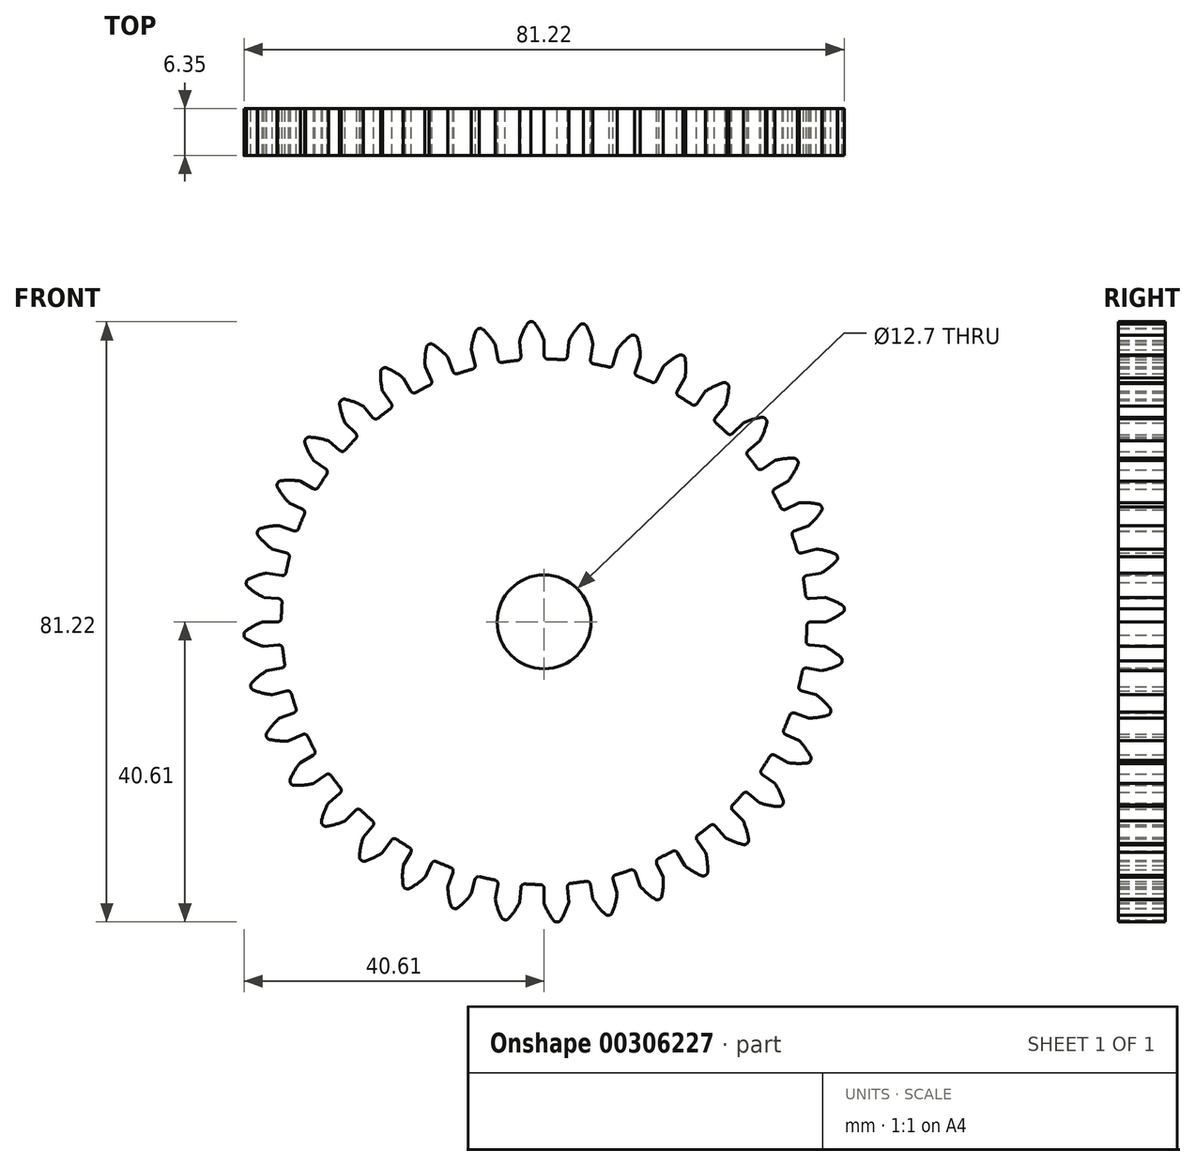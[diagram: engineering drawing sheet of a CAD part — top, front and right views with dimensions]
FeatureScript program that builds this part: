
annotation { "Feature Type Name" : "Feature", "Feature Type Description" : "" }
export const myFeature = defineFeature(function(context is Context, id is Id, definition is map)
    precondition{}
    {
        {
            var Q0;
            Q0=qCreatedBy(makeId("Front.planeOp"),FACE);
            var sketch = newSketch(context, id + "F0", { "sketchPlane" : qUnion([Q0])});
            skArc(sketch, "E0", {"start": v(-3.6, 35.38) * mm, "mid": v(1.55, -35.53) * mm, "end": v(0.5, 35.56) * mm});
            skLineSegment(sketch, "E1", {"start": v(0, 0) * mm, "end": v(-2.87, 65.75) * mm, "construction": true});
            skArc(sketch, "E2", {"start": v(0, 38.1) * mm, "mid": v(-0.56, 39.3) * mm, "end": v(-1.28, 40.41) * mm});
            skLineSegment(sketch, "E3", {"start": v(-1.69, 40.61) * mm, "end": v(-1.77, 40.61) * mm});
            skLineSegment(sketch, "E4", {"start": v(0, 38.1) * mm, "end": v(0, 36.06) * mm});
            skLineSegment(sketch, "E5.MirrorCS", {"start": v(-1.86, 40.6) * mm, "end": v(-1.77, 40.61) * mm});
            skArc(sketch, "E6.MirrorCS", {"start": v(-3.32, 37.96) * mm, "mid": v(-2.87, 39.2) * mm, "end": v(-2.24, 40.37) * mm});
            skLineSegment(sketch, "E7.MirrorCS", {"start": v(-3.32, 37.96) * mm, "end": v(-3.14, 35.93) * mm});
            skPoint(sketch, "E8.orphan", {"position": v(-2.9, 33.08) * mm});
            skPoint(sketch, "E9.orphan", {"position": v(0, 33.2) * mm});
            skPoint(sketch, "E10.visualSharp", {"position": v(-3.1, 35.42) * mm});
            skArc(sketch, "E10.filletArc", {"start": v(-3.6, 35.38) * mm, "mid": v(-3.26, 35.56) * mm, "end": v(-3.14, 35.93) * mm});
            skPoint(sketch, "E11.visualSharp", {"position": v(0, 35.56) * mm});
            skArc(sketch, "E11.filletArc", {"start": v(0, 36.06) * mm, "mid": v(0.15, 35.7) * mm, "end": v(0.5, 35.56) * mm});
            skPoint(sketch, "E12.visualSharp", {"position": v(-2.1, 40.59) * mm});
            skArc(sketch, "E12.filletArc", {"start": v(-1.86, 40.6) * mm, "mid": v(-2.08, 40.53) * mm, "end": v(-2.24, 40.37) * mm});
            skPoint(sketch, "E13.visualSharp", {"position": v(-1.44, 40.61) * mm});
            skArc(sketch, "E13.filletArc", {"start": v(-1.28, 40.41) * mm, "mid": v(-1.46, 40.56) * mm, "end": v(-1.69, 40.61) * mm});
            skArc(sketch, "E14.1.0", {"start": v(-9.69, 34.22) * mm, "mid": v(-9.38, 34.45) * mm, "end": v(-9.33, 34.84) * mm});
            skLineSegment(sketch, "E14.1.1", {"start": v(-9.86, 36.8) * mm, "end": v(-9.33, 34.84) * mm});
            skArc(sketch, "E14.1.2", {"start": v(-9.86, 36.8) * mm, "mid": v(-9.63, 38.1) * mm, "end": v(-9.22, 39.37) * mm});
            skArc(sketch, "E14.1.3", {"start": v(-6.62, 37.52) * mm, "mid": v(-7.38, 38.6) * mm, "end": v(-8.28, 39.58) * mm});
            skArc(sketch, "E14.1.4", {"start": v(-6.26, 35.52) * mm, "mid": v(-6.06, 35.2) * mm, "end": v(-5.68, 35.1) * mm});
            skLineSegment(sketch, "E14.1.5", {"start": v(-6.62, 37.52) * mm, "end": v(-6.26, 35.52) * mm});
            skArc(sketch, "E14.1.6", {"start": v(-8.88, 39.67) * mm, "mid": v(-9.09, 39.56) * mm, "end": v(-9.22, 39.37) * mm});
            skLineSegment(sketch, "E14.1.7", {"start": v(-8.88, 39.67) * mm, "end": v(-8.8, 39.69) * mm});
            skLineSegment(sketch, "E14.1.8", {"start": v(-8.72, 39.7) * mm, "end": v(-8.8, 39.69) * mm});
            skArc(sketch, "E14.1.9", {"start": v(-8.28, 39.58) * mm, "mid": v(-8.48, 39.7) * mm, "end": v(-8.72, 39.7) * mm});
            skArc(sketch, "E14.2.0", {"start": v(-15.48, 32.01) * mm, "mid": v(-15.22, 32.3) * mm, "end": v(-15.24, 32.69) * mm});
            skLineSegment(sketch, "E14.2.1", {"start": v(-16.1, 34.53) * mm, "end": v(-15.24, 32.69) * mm});
            skArc(sketch, "E14.2.2", {"start": v(-16.1, 34.53) * mm, "mid": v(-16.1, 35.86) * mm, "end": v(-15.92, 37.17) * mm});
            skArc(sketch, "E14.2.3", {"start": v(-13.03, 35.8) * mm, "mid": v(-13.97, 36.74) * mm, "end": v(-15.03, 37.54) * mm});
            skArc(sketch, "E14.2.4", {"start": v(-12.33, 33.89) * mm, "mid": v(-12.08, 33.6) * mm, "end": v(-11.7, 33.58) * mm});
            skLineSegment(sketch, "E14.2.5", {"start": v(-13.03, 35.8) * mm, "end": v(-12.33, 33.89) * mm});
            skArc(sketch, "E14.2.6", {"start": v(-15.63, 37.52) * mm, "mid": v(-15.82, 37.38) * mm, "end": v(-15.92, 37.17) * mm});
            skLineSegment(sketch, "E14.2.7", {"start": v(-15.63, 37.52) * mm, "end": v(-15.56, 37.56) * mm});
            skLineSegment(sketch, "E14.2.8", {"start": v(-15.48, 37.59) * mm, "end": v(-15.56, 37.56) * mm});
            skArc(sketch, "E14.2.9", {"start": v(-15.03, 37.54) * mm, "mid": v(-15.25, 37.62) * mm, "end": v(-15.48, 37.59) * mm});
            skArc(sketch, "E14.3.0", {"start": v(-20.8, 28.84) * mm, "mid": v(-20.6, 29.17) * mm, "end": v(-20.69, 29.54) * mm});
            skLineSegment(sketch, "E14.3.1", {"start": v(-21.85, 31.2) * mm, "end": v(-20.69, 29.54) * mm});
            skArc(sketch, "E14.3.2", {"start": v(-21.85, 31.2) * mm, "mid": v(-22.08, 32.51) * mm, "end": v(-22.13, 33.84) * mm});
            skArc(sketch, "E14.3.3", {"start": v(-19.05, 33) * mm, "mid": v(-20.14, 33.76) * mm, "end": v(-21.32, 34.36) * mm});
            skArc(sketch, "E14.3.4", {"start": v(-18.03, 31.23) * mm, "mid": v(-17.73, 31) * mm, "end": v(-17.34, 31.04) * mm});
            skLineSegment(sketch, "E14.3.5", {"start": v(-19.05, 33) * mm, "end": v(-18.03, 31.23) * mm});
            skArc(sketch, "E14.3.6", {"start": v(-21.91, 34.24) * mm, "mid": v(-22.07, 34.06) * mm, "end": v(-22.13, 33.84) * mm});
            skLineSegment(sketch, "E14.3.7", {"start": v(-21.91, 34.24) * mm, "end": v(-21.84, 34.29) * mm});
            skLineSegment(sketch, "E14.3.8", {"start": v(-21.77, 34.33) * mm, "end": v(-21.84, 34.29) * mm});
            skArc(sketch, "E14.3.9", {"start": v(-21.32, 34.36) * mm, "mid": v(-21.55, 34.4) * mm, "end": v(-21.77, 34.33) * mm});
            skArc(sketch, "E14.4.0", {"start": v(-25.5, 24.79) * mm, "mid": v(-25.35, 25.15) * mm, "end": v(-25.5, 25.5) * mm});
            skLineSegment(sketch, "E14.4.1", {"start": v(-26.94, 26.94) * mm, "end": v(-25.5, 25.5) * mm});
            skArc(sketch, "E14.4.2", {"start": v(-26.94, 26.94) * mm, "mid": v(-27.4, 28.19) * mm, "end": v(-27.67, 29.48) * mm});
            skArc(sketch, "E14.4.3", {"start": v(-24.5, 29.19) * mm, "mid": v(-25.7, 29.75) * mm, "end": v(-26.96, 30.13) * mm});
            skArc(sketch, "E14.4.4", {"start": v(-23.18, 27.63) * mm, "mid": v(-22.84, 27.45) * mm, "end": v(-22.47, 27.56) * mm});
            skLineSegment(sketch, "E14.4.5", {"start": v(-24.5, 29.19) * mm, "end": v(-23.18, 27.63) * mm});
            skArc(sketch, "E14.4.6", {"start": v(-27.53, 29.91) * mm, "mid": v(-27.65, 29.71) * mm, "end": v(-27.67, 29.48) * mm});
            skLineSegment(sketch, "E14.4.7", {"start": v(-27.53, 29.91) * mm, "end": v(-27.46, 29.97) * mm});
            skLineSegment(sketch, "E14.4.8", {"start": v(-27.4, 30.03) * mm, "end": v(-27.46, 29.97) * mm});
            skArc(sketch, "E14.4.9", {"start": v(-26.96, 30.13) * mm, "mid": v(-27.2, 30.13) * mm, "end": v(-27.4, 30.03) * mm});
            skArc(sketch, "E14.5.0", {"start": v(-29.41, 19.98) * mm, "mid": v(-29.33, 20.36) * mm, "end": v(-29.54, 20.69) * mm});
            skLineSegment(sketch, "E14.5.1", {"start": v(-31.2, 21.85) * mm, "end": v(-29.54, 20.69) * mm});
            skArc(sketch, "E14.5.2", {"start": v(-31.2, 21.85) * mm, "mid": v(-31.87, 23) * mm, "end": v(-32.37, 24.23) * mm});
            skArc(sketch, "E14.5.3", {"start": v(-29.19, 24.5) * mm, "mid": v(-30.47, 24.83) * mm, "end": v(-31.78, 25) * mm});
            skArc(sketch, "E14.5.4", {"start": v(-27.63, 23.18) * mm, "mid": v(-27.26, 23.06) * mm, "end": v(-26.92, 23.24) * mm});
            skLineSegment(sketch, "E14.5.5", {"start": v(-29.19, 24.5) * mm, "end": v(-27.63, 23.18) * mm});
            skArc(sketch, "E14.5.6", {"start": v(-32.3, 24.68) * mm, "mid": v(-32.39, 24.46) * mm, "end": v(-32.37, 24.23) * mm});
            skLineSegment(sketch, "E14.5.7", {"start": v(-32.3, 24.68) * mm, "end": v(-32.25, 24.75) * mm});
            skLineSegment(sketch, "E14.5.8", {"start": v(-32.2, 24.81) * mm, "end": v(-32.25, 24.75) * mm});
            skArc(sketch, "E14.5.9", {"start": v(-31.78, 25) * mm, "mid": v(-32.01, 24.95) * mm, "end": v(-32.2, 24.81) * mm});
            skArc(sketch, "E14.6.0", {"start": v(-32.44, 14.57) * mm, "mid": v(-32.42, 14.96) * mm, "end": v(-32.69, 15.24) * mm});
            skLineSegment(sketch, "E14.6.1", {"start": v(-34.53, 16.1) * mm, "end": v(-32.69, 15.24) * mm});
            skArc(sketch, "E14.6.2", {"start": v(-34.53, 16.1) * mm, "mid": v(-35.38, 17.12) * mm, "end": v(-36.08, 18.24) * mm});
            skArc(sketch, "E14.6.3", {"start": v(-33, 19.05) * mm, "mid": v(-34.32, 19.16) * mm, "end": v(-35.64, 19.1) * mm});
            skArc(sketch, "E14.6.4", {"start": v(-31.23, 18.03) * mm, "mid": v(-30.85, 17.98) * mm, "end": v(-30.54, 18.21) * mm});
            skLineSegment(sketch, "E14.6.5", {"start": v(-33, 19.05) * mm, "end": v(-31.23, 18.03) * mm});
            skArc(sketch, "E14.6.6", {"start": v(-36.1, 18.7) * mm, "mid": v(-36.14, 18.47) * mm, "end": v(-36.08, 18.24) * mm});
            skLineSegment(sketch, "E14.6.7", {"start": v(-36.1, 18.7) * mm, "end": v(-36.06, 18.77) * mm});
            skLineSegment(sketch, "E14.6.8", {"start": v(-36.02, 18.85) * mm, "end": v(-36.06, 18.77) * mm});
            skArc(sketch, "E14.6.9", {"start": v(-35.64, 19.1) * mm, "mid": v(-35.86, 19.01) * mm, "end": v(-36.02, 18.85) * mm});
            skArc(sketch, "E14.7.0", {"start": v(-34.47, 8.72) * mm, "mid": v(-34.53, 9.1) * mm, "end": v(-34.84, 9.33) * mm});
            skLineSegment(sketch, "E14.7.1", {"start": v(-36.8, 9.86) * mm, "end": v(-34.84, 9.33) * mm});
            skArc(sketch, "E14.7.2", {"start": v(-36.8, 9.86) * mm, "mid": v(-37.82, 10.71) * mm, "end": v(-38.7, 11.7) * mm});
            skArc(sketch, "E14.7.3", {"start": v(-35.8, 13.03) * mm, "mid": v(-37.12, 12.91) * mm, "end": v(-38.41, 12.62) * mm});
            skArc(sketch, "E14.7.4", {"start": v(-33.89, 12.33) * mm, "mid": v(-33.5, 12.35) * mm, "end": v(-33.24, 12.63) * mm});
            skLineSegment(sketch, "E14.7.5", {"start": v(-35.8, 13.03) * mm, "end": v(-33.89, 12.33) * mm});
            skArc(sketch, "E14.7.6", {"start": v(-38.8, 12.14) * mm, "mid": v(-38.8, 11.9) * mm, "end": v(-38.7, 11.7) * mm});
            skLineSegment(sketch, "E14.7.7", {"start": v(-38.8, 12.14) * mm, "end": v(-38.77, 12.22) * mm});
            skLineSegment(sketch, "E14.7.8", {"start": v(-38.74, 12.3) * mm, "end": v(-38.77, 12.22) * mm});
            skArc(sketch, "E14.7.9", {"start": v(-38.41, 12.62) * mm, "mid": v(-38.61, 12.5) * mm, "end": v(-38.74, 12.3) * mm});
            skArc(sketch, "E14.8.0", {"start": v(-35.46, 2.6) * mm, "mid": v(-35.58, 2.97) * mm, "end": v(-35.93, 3.14) * mm});
            skLineSegment(sketch, "E14.8.1", {"start": v(-37.96, 3.32) * mm, "end": v(-35.93, 3.14) * mm});
            skArc(sketch, "E14.8.2", {"start": v(-37.96, 3.32) * mm, "mid": v(-39.1, 3.98) * mm, "end": v(-40.15, 4.8) * mm});
            skArc(sketch, "E14.8.3", {"start": v(-37.52, 6.62) * mm, "mid": v(-38.8, 6.27) * mm, "end": v(-40.02, 5.75) * mm});
            skArc(sketch, "E14.8.4", {"start": v(-35.52, 6.26) * mm, "mid": v(-35.14, 6.34) * mm, "end": v(-34.93, 6.67) * mm});
            skLineSegment(sketch, "E14.8.5", {"start": v(-37.52, 6.62) * mm, "end": v(-35.52, 6.26) * mm});
            skArc(sketch, "E14.8.6", {"start": v(-40.31, 5.22) * mm, "mid": v(-40.28, 5) * mm, "end": v(-40.15, 4.8) * mm});
            skLineSegment(sketch, "E14.8.7", {"start": v(-40.31, 5.22) * mm, "end": v(-40.3, 5.3) * mm});
            skLineSegment(sketch, "E14.8.8", {"start": v(-40.3, 5.4) * mm, "end": v(-40.3, 5.3) * mm});
            skArc(sketch, "E14.8.9", {"start": v(-40.02, 5.75) * mm, "mid": v(-40.2, 5.6) * mm, "end": v(-40.3, 5.4) * mm});
            skArc(sketch, "E14.9.0", {"start": v(-35.38, -3.6) * mm, "mid": v(-35.56, -3.26) * mm, "end": v(-35.93, -3.14) * mm});
            skLineSegment(sketch, "E14.9.1", {"start": v(-37.96, -3.32) * mm, "end": v(-35.93, -3.14) * mm});
            skArc(sketch, "E14.9.2", {"start": v(-37.96, -3.32) * mm, "mid": v(-39.2, -2.87) * mm, "end": v(-40.37, -2.24) * mm});
            skArc(sketch, "E14.9.3", {"start": v(-38.1, 0) * mm, "mid": v(-39.3, -0.56) * mm, "end": v(-40.41, -1.28) * mm});
            skArc(sketch, "E14.9.4", {"start": v(-36.06, 0) * mm, "mid": v(-35.7, 0.15) * mm, "end": v(-35.56, 0.5) * mm});
            skLineSegment(sketch, "E14.9.5", {"start": v(-38.1, 0) * mm, "end": v(-36.06, 0) * mm});
            skArc(sketch, "E14.9.6", {"start": v(-40.6, -1.86) * mm, "mid": v(-40.53, -2.08) * mm, "end": v(-40.37, -2.24) * mm});
            skLineSegment(sketch, "E14.9.7", {"start": v(-40.6, -1.86) * mm, "end": v(-40.61, -1.77) * mm});
            skLineSegment(sketch, "E14.9.8", {"start": v(-40.61, -1.69) * mm, "end": v(-40.61, -1.77) * mm});
            skArc(sketch, "E14.9.9", {"start": v(-40.41, -1.28) * mm, "mid": v(-40.56, -1.46) * mm, "end": v(-40.61, -1.69) * mm});
            skArc(sketch, "E14.10.0", {"start": v(-34.22, -9.69) * mm, "mid": v(-34.45, -9.38) * mm, "end": v(-34.84, -9.33) * mm});
            skLineSegment(sketch, "E14.10.1", {"start": v(-36.8, -9.86) * mm, "end": v(-34.84, -9.33) * mm});
            skArc(sketch, "E14.10.2", {"start": v(-36.8, -9.86) * mm, "mid": v(-38.1, -9.63) * mm, "end": v(-39.37, -9.22) * mm});
            skArc(sketch, "E14.10.3", {"start": v(-37.52, -6.62) * mm, "mid": v(-38.6, -7.38) * mm, "end": v(-39.58, -8.28) * mm});
            skArc(sketch, "E14.10.4", {"start": v(-35.52, -6.26) * mm, "mid": v(-35.2, -6.06) * mm, "end": v(-35.1, -5.68) * mm});
            skLineSegment(sketch, "E14.10.5", {"start": v(-37.52, -6.62) * mm, "end": v(-35.52, -6.26) * mm});
            skArc(sketch, "E14.10.6", {"start": v(-39.67, -8.88) * mm, "mid": v(-39.56, -9.09) * mm, "end": v(-39.37, -9.22) * mm});
            skLineSegment(sketch, "E14.10.7", {"start": v(-39.67, -8.88) * mm, "end": v(-39.69, -8.8) * mm});
            skLineSegment(sketch, "E14.10.8", {"start": v(-39.7, -8.72) * mm, "end": v(-39.69, -8.8) * mm});
            skArc(sketch, "E14.10.9", {"start": v(-39.58, -8.28) * mm, "mid": v(-39.7, -8.48) * mm, "end": v(-39.7, -8.72) * mm});
            skArc(sketch, "E14.11.0", {"start": v(-32.01, -15.48) * mm, "mid": v(-32.3, -15.22) * mm, "end": v(-32.69, -15.24) * mm});
            skLineSegment(sketch, "E14.11.1", {"start": v(-34.53, -16.1) * mm, "end": v(-32.69, -15.24) * mm});
            skArc(sketch, "E14.11.2", {"start": v(-34.53, -16.1) * mm, "mid": v(-35.86, -16.1) * mm, "end": v(-37.17, -15.92) * mm});
            skArc(sketch, "E14.11.3", {"start": v(-35.8, -13.03) * mm, "mid": v(-36.74, -13.97) * mm, "end": v(-37.54, -15.03) * mm});
            skArc(sketch, "E14.11.4", {"start": v(-33.89, -12.33) * mm, "mid": v(-33.6, -12.08) * mm, "end": v(-33.58, -11.7) * mm});
            skLineSegment(sketch, "E14.11.5", {"start": v(-35.8, -13.03) * mm, "end": v(-33.89, -12.33) * mm});
            skArc(sketch, "E14.11.6", {"start": v(-37.52, -15.63) * mm, "mid": v(-37.38, -15.82) * mm, "end": v(-37.17, -15.92) * mm});
            skLineSegment(sketch, "E14.11.7", {"start": v(-37.52, -15.63) * mm, "end": v(-37.56, -15.56) * mm});
            skLineSegment(sketch, "E14.11.8", {"start": v(-37.59, -15.48) * mm, "end": v(-37.56, -15.56) * mm});
            skArc(sketch, "E14.11.9", {"start": v(-37.54, -15.03) * mm, "mid": v(-37.62, -15.25) * mm, "end": v(-37.59, -15.48) * mm});
            skArc(sketch, "E14.12.0", {"start": v(-28.84, -20.8) * mm, "mid": v(-29.17, -20.6) * mm, "end": v(-29.54, -20.69) * mm});
            skLineSegment(sketch, "E14.12.1", {"start": v(-31.2, -21.85) * mm, "end": v(-29.54, -20.69) * mm});
            skArc(sketch, "E14.12.2", {"start": v(-31.2, -21.85) * mm, "mid": v(-32.51, -22.08) * mm, "end": v(-33.84, -22.13) * mm});
            skArc(sketch, "E14.12.3", {"start": v(-33, -19.05) * mm, "mid": v(-33.76, -20.14) * mm, "end": v(-34.36, -21.32) * mm});
            skArc(sketch, "E14.12.4", {"start": v(-31.23, -18.03) * mm, "mid": v(-31, -17.73) * mm, "end": v(-31.04, -17.34) * mm});
            skLineSegment(sketch, "E14.12.5", {"start": v(-33, -19.05) * mm, "end": v(-31.23, -18.03) * mm});
            skArc(sketch, "E14.12.6", {"start": v(-34.24, -21.91) * mm, "mid": v(-34.06, -22.07) * mm, "end": v(-33.84, -22.13) * mm});
            skLineSegment(sketch, "E14.12.7", {"start": v(-34.24, -21.91) * mm, "end": v(-34.29, -21.84) * mm});
            skLineSegment(sketch, "E14.12.8", {"start": v(-34.33, -21.77) * mm, "end": v(-34.29, -21.84) * mm});
            skArc(sketch, "E14.12.9", {"start": v(-34.36, -21.32) * mm, "mid": v(-34.4, -21.55) * mm, "end": v(-34.33, -21.77) * mm});
            skArc(sketch, "E14.13.0", {"start": v(-24.79, -25.5) * mm, "mid": v(-25.15, -25.35) * mm, "end": v(-25.5, -25.5) * mm});
            skLineSegment(sketch, "E14.13.1", {"start": v(-26.94, -26.94) * mm, "end": v(-25.5, -25.5) * mm});
            skArc(sketch, "E14.13.2", {"start": v(-26.94, -26.94) * mm, "mid": v(-28.19, -27.4) * mm, "end": v(-29.48, -27.67) * mm});
            skArc(sketch, "E14.13.3", {"start": v(-29.19, -24.5) * mm, "mid": v(-29.75, -25.7) * mm, "end": v(-30.13, -26.96) * mm});
            skArc(sketch, "E14.13.4", {"start": v(-27.63, -23.18) * mm, "mid": v(-27.45, -22.84) * mm, "end": v(-27.56, -22.47) * mm});
            skLineSegment(sketch, "E14.13.5", {"start": v(-29.19, -24.5) * mm, "end": v(-27.63, -23.18) * mm});
            skArc(sketch, "E14.13.6", {"start": v(-29.91, -27.53) * mm, "mid": v(-29.71, -27.65) * mm, "end": v(-29.48, -27.67) * mm});
            skLineSegment(sketch, "E14.13.7", {"start": v(-29.91, -27.53) * mm, "end": v(-29.97, -27.46) * mm});
            skLineSegment(sketch, "E14.13.8", {"start": v(-30.03, -27.4) * mm, "end": v(-29.97, -27.46) * mm});
            skArc(sketch, "E14.13.9", {"start": v(-30.13, -26.96) * mm, "mid": v(-30.13, -27.2) * mm, "end": v(-30.03, -27.4) * mm});
            skArc(sketch, "E14.14.0", {"start": v(-19.98, -29.41) * mm, "mid": v(-20.36, -29.33) * mm, "end": v(-20.69, -29.54) * mm});
            skLineSegment(sketch, "E14.14.1", {"start": v(-21.85, -31.2) * mm, "end": v(-20.69, -29.54) * mm});
            skArc(sketch, "E14.14.2", {"start": v(-21.85, -31.2) * mm, "mid": v(-23, -31.87) * mm, "end": v(-24.23, -32.37) * mm});
            skArc(sketch, "E14.14.3", {"start": v(-24.5, -29.19) * mm, "mid": v(-24.83, -30.47) * mm, "end": v(-25, -31.78) * mm});
            skArc(sketch, "E14.14.4", {"start": v(-23.18, -27.63) * mm, "mid": v(-23.06, -27.26) * mm, "end": v(-23.24, -26.92) * mm});
            skLineSegment(sketch, "E14.14.5", {"start": v(-24.5, -29.19) * mm, "end": v(-23.18, -27.63) * mm});
            skArc(sketch, "E14.14.6", {"start": v(-24.68, -32.3) * mm, "mid": v(-24.46, -32.39) * mm, "end": v(-24.23, -32.37) * mm});
            skLineSegment(sketch, "E14.14.7", {"start": v(-24.68, -32.3) * mm, "end": v(-24.75, -32.25) * mm});
            skLineSegment(sketch, "E14.14.8", {"start": v(-24.81, -32.2) * mm, "end": v(-24.75, -32.25) * mm});
            skArc(sketch, "E14.14.9", {"start": v(-25, -31.78) * mm, "mid": v(-24.95, -32.01) * mm, "end": v(-24.81, -32.2) * mm});
            skArc(sketch, "E14.15.0", {"start": v(-14.57, -32.44) * mm, "mid": v(-14.96, -32.42) * mm, "end": v(-15.24, -32.69) * mm});
            skLineSegment(sketch, "E14.15.1", {"start": v(-16.1, -34.53) * mm, "end": v(-15.24, -32.69) * mm});
            skArc(sketch, "E14.15.2", {"start": v(-16.1, -34.53) * mm, "mid": v(-17.12, -35.38) * mm, "end": v(-18.24, -36.08) * mm});
            skArc(sketch, "E14.15.3", {"start": v(-19.05, -33) * mm, "mid": v(-19.16, -34.32) * mm, "end": v(-19.1, -35.64) * mm});
            skArc(sketch, "E14.15.4", {"start": v(-18.03, -31.23) * mm, "mid": v(-17.98, -30.85) * mm, "end": v(-18.21, -30.54) * mm});
            skLineSegment(sketch, "E14.15.5", {"start": v(-19.05, -33) * mm, "end": v(-18.03, -31.23) * mm});
            skArc(sketch, "E14.15.6", {"start": v(-18.7, -36.1) * mm, "mid": v(-18.47, -36.14) * mm, "end": v(-18.24, -36.08) * mm});
            skLineSegment(sketch, "E14.15.7", {"start": v(-18.7, -36.1) * mm, "end": v(-18.77, -36.06) * mm});
            skLineSegment(sketch, "E14.15.8", {"start": v(-18.85, -36.02) * mm, "end": v(-18.77, -36.06) * mm});
            skArc(sketch, "E14.15.9", {"start": v(-19.1, -35.64) * mm, "mid": v(-19.01, -35.86) * mm, "end": v(-18.85, -36.02) * mm});
            skArc(sketch, "E14.16.0", {"start": v(-8.72, -34.47) * mm, "mid": v(-9.1, -34.53) * mm, "end": v(-9.33, -34.84) * mm});
            skLineSegment(sketch, "E14.16.1", {"start": v(-9.86, -36.8) * mm, "end": v(-9.33, -34.84) * mm});
            skArc(sketch, "E14.16.2", {"start": v(-9.86, -36.8) * mm, "mid": v(-10.71, -37.82) * mm, "end": v(-11.7, -38.7) * mm});
            skArc(sketch, "E14.16.3", {"start": v(-13.03, -35.8) * mm, "mid": v(-12.91, -37.12) * mm, "end": v(-12.62, -38.41) * mm});
            skArc(sketch, "E14.16.4", {"start": v(-12.33, -33.89) * mm, "mid": v(-12.35, -33.5) * mm, "end": v(-12.63, -33.24) * mm});
            skLineSegment(sketch, "E14.16.5", {"start": v(-13.03, -35.8) * mm, "end": v(-12.33, -33.89) * mm});
            skArc(sketch, "E14.16.6", {"start": v(-12.14, -38.8) * mm, "mid": v(-11.9, -38.8) * mm, "end": v(-11.7, -38.7) * mm});
            skLineSegment(sketch, "E14.16.7", {"start": v(-12.14, -38.8) * mm, "end": v(-12.22, -38.77) * mm});
            skLineSegment(sketch, "E14.16.8", {"start": v(-12.3, -38.74) * mm, "end": v(-12.22, -38.77) * mm});
            skArc(sketch, "E14.16.9", {"start": v(-12.62, -38.41) * mm, "mid": v(-12.5, -38.61) * mm, "end": v(-12.3, -38.74) * mm});
            skArc(sketch, "E14.17.0", {"start": v(-2.6, -35.46) * mm, "mid": v(-2.97, -35.58) * mm, "end": v(-3.14, -35.93) * mm});
            skLineSegment(sketch, "E14.17.1", {"start": v(-3.32, -37.96) * mm, "end": v(-3.14, -35.93) * mm});
            skArc(sketch, "E14.17.2", {"start": v(-3.32, -37.96) * mm, "mid": v(-3.98, -39.1) * mm, "end": v(-4.8, -40.15) * mm});
            skArc(sketch, "E14.17.3", {"start": v(-6.62, -37.52) * mm, "mid": v(-6.27, -38.8) * mm, "end": v(-5.75, -40.02) * mm});
            skArc(sketch, "E14.17.4", {"start": v(-6.26, -35.52) * mm, "mid": v(-6.34, -35.14) * mm, "end": v(-6.67, -34.93) * mm});
            skLineSegment(sketch, "E14.17.5", {"start": v(-6.62, -37.52) * mm, "end": v(-6.26, -35.52) * mm});
            skArc(sketch, "E14.17.6", {"start": v(-5.22, -40.31) * mm, "mid": v(-5, -40.28) * mm, "end": v(-4.8, -40.15) * mm});
            skLineSegment(sketch, "E14.17.7", {"start": v(-5.22, -40.31) * mm, "end": v(-5.3, -40.3) * mm});
            skLineSegment(sketch, "E14.17.8", {"start": v(-5.4, -40.3) * mm, "end": v(-5.3, -40.3) * mm});
            skArc(sketch, "E14.17.9", {"start": v(-5.75, -40.02) * mm, "mid": v(-5.6, -40.2) * mm, "end": v(-5.4, -40.3) * mm});
            skArc(sketch, "E14.18.0", {"start": v(3.6, -35.38) * mm, "mid": v(3.26, -35.56) * mm, "end": v(3.14, -35.93) * mm});
            skLineSegment(sketch, "E14.18.1", {"start": v(3.32, -37.96) * mm, "end": v(3.14, -35.93) * mm});
            skArc(sketch, "E14.18.2", {"start": v(3.32, -37.96) * mm, "mid": v(2.87, -39.2) * mm, "end": v(2.24, -40.37) * mm});
            skArc(sketch, "E14.18.3", {"start": v(0, -38.1) * mm, "mid": v(0.56, -39.3) * mm, "end": v(1.28, -40.41) * mm});
            skArc(sketch, "E14.18.4", {"start": v(0, -36.06) * mm, "mid": v(-0.15, -35.7) * mm, "end": v(-0.5, -35.56) * mm});
            skLineSegment(sketch, "E14.18.5", {"start": v(0, -38.1) * mm, "end": v(0, -36.06) * mm});
            skArc(sketch, "E14.18.6", {"start": v(1.86, -40.6) * mm, "mid": v(2.08, -40.53) * mm, "end": v(2.24, -40.37) * mm});
            skLineSegment(sketch, "E14.18.7", {"start": v(1.86, -40.6) * mm, "end": v(1.77, -40.61) * mm});
            skLineSegment(sketch, "E14.18.8", {"start": v(1.69, -40.61) * mm, "end": v(1.77, -40.61) * mm});
            skArc(sketch, "E14.18.9", {"start": v(1.28, -40.41) * mm, "mid": v(1.46, -40.56) * mm, "end": v(1.69, -40.61) * mm});
            skArc(sketch, "E14.19.0", {"start": v(9.69, -34.22) * mm, "mid": v(9.38, -34.45) * mm, "end": v(9.33, -34.84) * mm});
            skLineSegment(sketch, "E14.19.1", {"start": v(9.86, -36.8) * mm, "end": v(9.33, -34.84) * mm});
            skArc(sketch, "E14.19.2", {"start": v(9.86, -36.8) * mm, "mid": v(9.63, -38.1) * mm, "end": v(9.22, -39.37) * mm});
            skArc(sketch, "E14.19.3", {"start": v(6.62, -37.52) * mm, "mid": v(7.38, -38.6) * mm, "end": v(8.28, -39.58) * mm});
            skArc(sketch, "E14.19.4", {"start": v(6.26, -35.52) * mm, "mid": v(6.06, -35.2) * mm, "end": v(5.68, -35.1) * mm});
            skLineSegment(sketch, "E14.19.5", {"start": v(6.62, -37.52) * mm, "end": v(6.26, -35.52) * mm});
            skArc(sketch, "E14.19.6", {"start": v(8.88, -39.67) * mm, "mid": v(9.09, -39.56) * mm, "end": v(9.22, -39.37) * mm});
            skLineSegment(sketch, "E14.19.7", {"start": v(8.88, -39.67) * mm, "end": v(8.8, -39.69) * mm});
            skLineSegment(sketch, "E14.19.8", {"start": v(8.72, -39.7) * mm, "end": v(8.8, -39.69) * mm});
            skArc(sketch, "E14.19.9", {"start": v(8.28, -39.58) * mm, "mid": v(8.48, -39.7) * mm, "end": v(8.72, -39.7) * mm});
            skArc(sketch, "E14.20.0", {"start": v(15.48, -32.01) * mm, "mid": v(15.22, -32.3) * mm, "end": v(15.24, -32.69) * mm});
            skLineSegment(sketch, "E14.20.1", {"start": v(16.1, -34.53) * mm, "end": v(15.24, -32.69) * mm});
            skArc(sketch, "E14.20.2", {"start": v(16.1, -34.53) * mm, "mid": v(16.1, -35.86) * mm, "end": v(15.92, -37.17) * mm});
            skArc(sketch, "E14.20.3", {"start": v(13.03, -35.8) * mm, "mid": v(13.97, -36.74) * mm, "end": v(15.03, -37.54) * mm});
            skArc(sketch, "E14.20.4", {"start": v(12.33, -33.89) * mm, "mid": v(12.08, -33.6) * mm, "end": v(11.7, -33.58) * mm});
            skLineSegment(sketch, "E14.20.5", {"start": v(13.03, -35.8) * mm, "end": v(12.33, -33.89) * mm});
            skArc(sketch, "E14.20.6", {"start": v(15.63, -37.52) * mm, "mid": v(15.82, -37.38) * mm, "end": v(15.92, -37.17) * mm});
            skLineSegment(sketch, "E14.20.7", {"start": v(15.63, -37.52) * mm, "end": v(15.56, -37.56) * mm});
            skLineSegment(sketch, "E14.20.8", {"start": v(15.48, -37.59) * mm, "end": v(15.56, -37.56) * mm});
            skArc(sketch, "E14.20.9", {"start": v(15.03, -37.54) * mm, "mid": v(15.25, -37.62) * mm, "end": v(15.48, -37.59) * mm});
            skArc(sketch, "E14.21.0", {"start": v(20.8, -28.84) * mm, "mid": v(20.6, -29.17) * mm, "end": v(20.69, -29.54) * mm});
            skLineSegment(sketch, "E14.21.1", {"start": v(21.85, -31.2) * mm, "end": v(20.69, -29.54) * mm});
            skArc(sketch, "E14.21.2", {"start": v(21.85, -31.2) * mm, "mid": v(22.08, -32.51) * mm, "end": v(22.13, -33.84) * mm});
            skArc(sketch, "E14.21.3", {"start": v(19.05, -33) * mm, "mid": v(20.14, -33.76) * mm, "end": v(21.32, -34.36) * mm});
            skArc(sketch, "E14.21.4", {"start": v(18.03, -31.23) * mm, "mid": v(17.73, -31) * mm, "end": v(17.34, -31.04) * mm});
            skLineSegment(sketch, "E14.21.5", {"start": v(19.05, -33) * mm, "end": v(18.03, -31.23) * mm});
            skArc(sketch, "E14.21.6", {"start": v(21.91, -34.24) * mm, "mid": v(22.07, -34.06) * mm, "end": v(22.13, -33.84) * mm});
            skLineSegment(sketch, "E14.21.7", {"start": v(21.91, -34.24) * mm, "end": v(21.84, -34.29) * mm});
            skLineSegment(sketch, "E14.21.8", {"start": v(21.77, -34.33) * mm, "end": v(21.84, -34.29) * mm});
            skArc(sketch, "E14.21.9", {"start": v(21.32, -34.36) * mm, "mid": v(21.55, -34.4) * mm, "end": v(21.77, -34.33) * mm});
            skArc(sketch, "E14.22.0", {"start": v(25.5, -24.79) * mm, "mid": v(25.35, -25.15) * mm, "end": v(25.5, -25.5) * mm});
            skLineSegment(sketch, "E14.22.1", {"start": v(26.94, -26.94) * mm, "end": v(25.5, -25.5) * mm});
            skArc(sketch, "E14.22.2", {"start": v(26.94, -26.94) * mm, "mid": v(27.4, -28.19) * mm, "end": v(27.67, -29.48) * mm});
            skArc(sketch, "E14.22.3", {"start": v(24.5, -29.19) * mm, "mid": v(25.7, -29.75) * mm, "end": v(26.96, -30.13) * mm});
            skArc(sketch, "E14.22.4", {"start": v(23.18, -27.63) * mm, "mid": v(22.84, -27.45) * mm, "end": v(22.47, -27.56) * mm});
            skLineSegment(sketch, "E14.22.5", {"start": v(24.5, -29.19) * mm, "end": v(23.18, -27.63) * mm});
            skArc(sketch, "E14.22.6", {"start": v(27.53, -29.91) * mm, "mid": v(27.65, -29.71) * mm, "end": v(27.67, -29.48) * mm});
            skLineSegment(sketch, "E14.22.7", {"start": v(27.53, -29.91) * mm, "end": v(27.46, -29.97) * mm});
            skLineSegment(sketch, "E14.22.8", {"start": v(27.4, -30.03) * mm, "end": v(27.46, -29.97) * mm});
            skArc(sketch, "E14.22.9", {"start": v(26.96, -30.13) * mm, "mid": v(27.2, -30.13) * mm, "end": v(27.4, -30.03) * mm});
            skArc(sketch, "E14.23.0", {"start": v(29.41, -19.98) * mm, "mid": v(29.33, -20.36) * mm, "end": v(29.54, -20.69) * mm});
            skLineSegment(sketch, "E14.23.1", {"start": v(31.2, -21.85) * mm, "end": v(29.54, -20.69) * mm});
            skArc(sketch, "E14.23.2", {"start": v(31.2, -21.85) * mm, "mid": v(31.87, -23) * mm, "end": v(32.37, -24.23) * mm});
            skArc(sketch, "E14.23.3", {"start": v(29.19, -24.5) * mm, "mid": v(30.47, -24.83) * mm, "end": v(31.78, -25) * mm});
            skArc(sketch, "E14.23.4", {"start": v(27.63, -23.18) * mm, "mid": v(27.26, -23.06) * mm, "end": v(26.92, -23.24) * mm});
            skLineSegment(sketch, "E14.23.5", {"start": v(29.19, -24.5) * mm, "end": v(27.63, -23.18) * mm});
            skArc(sketch, "E14.23.6", {"start": v(32.3, -24.68) * mm, "mid": v(32.39, -24.46) * mm, "end": v(32.37, -24.23) * mm});
            skLineSegment(sketch, "E14.23.7", {"start": v(32.3, -24.68) * mm, "end": v(32.25, -24.75) * mm});
            skLineSegment(sketch, "E14.23.8", {"start": v(32.2, -24.81) * mm, "end": v(32.25, -24.75) * mm});
            skArc(sketch, "E14.23.9", {"start": v(31.78, -25) * mm, "mid": v(32.01, -24.95) * mm, "end": v(32.2, -24.81) * mm});
            skArc(sketch, "E14.24.0", {"start": v(32.44, -14.57) * mm, "mid": v(32.42, -14.96) * mm, "end": v(32.69, -15.24) * mm});
            skLineSegment(sketch, "E14.24.1", {"start": v(34.53, -16.1) * mm, "end": v(32.69, -15.24) * mm});
            skArc(sketch, "E14.24.2", {"start": v(34.53, -16.1) * mm, "mid": v(35.38, -17.12) * mm, "end": v(36.08, -18.24) * mm});
            skArc(sketch, "E14.24.3", {"start": v(33, -19.05) * mm, "mid": v(34.32, -19.16) * mm, "end": v(35.64, -19.1) * mm});
            skArc(sketch, "E14.24.4", {"start": v(31.23, -18.03) * mm, "mid": v(30.85, -17.98) * mm, "end": v(30.54, -18.21) * mm});
            skLineSegment(sketch, "E14.24.5", {"start": v(33, -19.05) * mm, "end": v(31.23, -18.03) * mm});
            skArc(sketch, "E14.24.6", {"start": v(36.1, -18.7) * mm, "mid": v(36.14, -18.47) * mm, "end": v(36.08, -18.24) * mm});
            skLineSegment(sketch, "E14.24.7", {"start": v(36.1, -18.7) * mm, "end": v(36.06, -18.77) * mm});
            skLineSegment(sketch, "E14.24.8", {"start": v(36.02, -18.85) * mm, "end": v(36.06, -18.77) * mm});
            skArc(sketch, "E14.24.9", {"start": v(35.64, -19.1) * mm, "mid": v(35.86, -19.01) * mm, "end": v(36.02, -18.85) * mm});
            skArc(sketch, "E14.25.0", {"start": v(34.47, -8.72) * mm, "mid": v(34.53, -9.1) * mm, "end": v(34.84, -9.33) * mm});
            skLineSegment(sketch, "E14.25.1", {"start": v(36.8, -9.86) * mm, "end": v(34.84, -9.33) * mm});
            skArc(sketch, "E14.25.2", {"start": v(36.8, -9.86) * mm, "mid": v(37.82, -10.71) * mm, "end": v(38.7, -11.7) * mm});
            skArc(sketch, "E14.25.3", {"start": v(35.8, -13.03) * mm, "mid": v(37.12, -12.91) * mm, "end": v(38.41, -12.62) * mm});
            skArc(sketch, "E14.25.4", {"start": v(33.89, -12.33) * mm, "mid": v(33.5, -12.35) * mm, "end": v(33.24, -12.63) * mm});
            skLineSegment(sketch, "E14.25.5", {"start": v(35.8, -13.03) * mm, "end": v(33.89, -12.33) * mm});
            skArc(sketch, "E14.25.6", {"start": v(38.8, -12.14) * mm, "mid": v(38.8, -11.9) * mm, "end": v(38.7, -11.7) * mm});
            skLineSegment(sketch, "E14.25.7", {"start": v(38.8, -12.14) * mm, "end": v(38.77, -12.22) * mm});
            skLineSegment(sketch, "E14.25.8", {"start": v(38.74, -12.3) * mm, "end": v(38.77, -12.22) * mm});
            skArc(sketch, "E14.25.9", {"start": v(38.41, -12.62) * mm, "mid": v(38.61, -12.5) * mm, "end": v(38.74, -12.3) * mm});
            skArc(sketch, "E14.26.0", {"start": v(35.46, -2.6) * mm, "mid": v(35.58, -2.97) * mm, "end": v(35.93, -3.14) * mm});
            skLineSegment(sketch, "E14.26.1", {"start": v(37.96, -3.32) * mm, "end": v(35.93, -3.14) * mm});
            skArc(sketch, "E14.26.2", {"start": v(37.96, -3.32) * mm, "mid": v(39.1, -3.98) * mm, "end": v(40.15, -4.8) * mm});
            skArc(sketch, "E14.26.3", {"start": v(37.52, -6.62) * mm, "mid": v(38.8, -6.27) * mm, "end": v(40.02, -5.75) * mm});
            skArc(sketch, "E14.26.4", {"start": v(35.52, -6.26) * mm, "mid": v(35.14, -6.34) * mm, "end": v(34.93, -6.67) * mm});
            skLineSegment(sketch, "E14.26.5", {"start": v(37.52, -6.62) * mm, "end": v(35.52, -6.26) * mm});
            skArc(sketch, "E14.26.6", {"start": v(40.31, -5.22) * mm, "mid": v(40.28, -5) * mm, "end": v(40.15, -4.8) * mm});
            skLineSegment(sketch, "E14.26.7", {"start": v(40.31, -5.22) * mm, "end": v(40.3, -5.3) * mm});
            skLineSegment(sketch, "E14.26.8", {"start": v(40.3, -5.4) * mm, "end": v(40.3, -5.3) * mm});
            skArc(sketch, "E14.26.9", {"start": v(40.02, -5.75) * mm, "mid": v(40.2, -5.6) * mm, "end": v(40.3, -5.4) * mm});
            skArc(sketch, "E14.27.0", {"start": v(35.38, 3.6) * mm, "mid": v(35.56, 3.26) * mm, "end": v(35.93, 3.14) * mm});
            skLineSegment(sketch, "E14.27.1", {"start": v(37.96, 3.32) * mm, "end": v(35.93, 3.14) * mm});
            skArc(sketch, "E14.27.2", {"start": v(37.96, 3.32) * mm, "mid": v(39.2, 2.87) * mm, "end": v(40.37, 2.24) * mm});
            skArc(sketch, "E14.27.3", {"start": v(38.1, 0) * mm, "mid": v(39.3, 0.56) * mm, "end": v(40.41, 1.28) * mm});
            skArc(sketch, "E14.27.4", {"start": v(36.06, 0) * mm, "mid": v(35.7, -0.15) * mm, "end": v(35.56, -0.5) * mm});
            skLineSegment(sketch, "E14.27.5", {"start": v(38.1, 0) * mm, "end": v(36.06, 0) * mm});
            skArc(sketch, "E14.27.6", {"start": v(40.6, 1.86) * mm, "mid": v(40.53, 2.08) * mm, "end": v(40.37, 2.24) * mm});
            skLineSegment(sketch, "E14.27.7", {"start": v(40.6, 1.86) * mm, "end": v(40.61, 1.77) * mm});
            skLineSegment(sketch, "E14.27.8", {"start": v(40.61, 1.69) * mm, "end": v(40.61, 1.77) * mm});
            skArc(sketch, "E14.27.9", {"start": v(40.41, 1.28) * mm, "mid": v(40.56, 1.46) * mm, "end": v(40.61, 1.69) * mm});
            skArc(sketch, "E14.28.0", {"start": v(34.22, 9.69) * mm, "mid": v(34.45, 9.38) * mm, "end": v(34.84, 9.33) * mm});
            skLineSegment(sketch, "E14.28.1", {"start": v(36.8, 9.86) * mm, "end": v(34.84, 9.33) * mm});
            skArc(sketch, "E14.28.2", {"start": v(36.8, 9.86) * mm, "mid": v(38.1, 9.63) * mm, "end": v(39.37, 9.22) * mm});
            skArc(sketch, "E14.28.3", {"start": v(37.52, 6.62) * mm, "mid": v(38.6, 7.38) * mm, "end": v(39.58, 8.28) * mm});
            skArc(sketch, "E14.28.4", {"start": v(35.52, 6.26) * mm, "mid": v(35.2, 6.06) * mm, "end": v(35.1, 5.68) * mm});
            skLineSegment(sketch, "E14.28.5", {"start": v(37.52, 6.62) * mm, "end": v(35.52, 6.26) * mm});
            skArc(sketch, "E14.28.6", {"start": v(39.67, 8.88) * mm, "mid": v(39.56, 9.09) * mm, "end": v(39.37, 9.22) * mm});
            skLineSegment(sketch, "E14.28.7", {"start": v(39.67, 8.88) * mm, "end": v(39.69, 8.8) * mm});
            skLineSegment(sketch, "E14.28.8", {"start": v(39.7, 8.72) * mm, "end": v(39.69, 8.8) * mm});
            skArc(sketch, "E14.28.9", {"start": v(39.58, 8.28) * mm, "mid": v(39.7, 8.48) * mm, "end": v(39.7, 8.72) * mm});
            skArc(sketch, "E14.29.0", {"start": v(32.01, 15.48) * mm, "mid": v(32.3, 15.22) * mm, "end": v(32.69, 15.24) * mm});
            skLineSegment(sketch, "E14.29.1", {"start": v(34.53, 16.1) * mm, "end": v(32.69, 15.24) * mm});
            skArc(sketch, "E14.29.2", {"start": v(34.53, 16.1) * mm, "mid": v(35.86, 16.1) * mm, "end": v(37.17, 15.92) * mm});
            skArc(sketch, "E14.29.3", {"start": v(35.8, 13.03) * mm, "mid": v(36.74, 13.97) * mm, "end": v(37.54, 15.03) * mm});
            skArc(sketch, "E14.29.4", {"start": v(33.89, 12.33) * mm, "mid": v(33.6, 12.08) * mm, "end": v(33.58, 11.7) * mm});
            skLineSegment(sketch, "E14.29.5", {"start": v(35.8, 13.03) * mm, "end": v(33.89, 12.33) * mm});
            skArc(sketch, "E14.29.6", {"start": v(37.52, 15.63) * mm, "mid": v(37.38, 15.82) * mm, "end": v(37.17, 15.92) * mm});
            skLineSegment(sketch, "E14.29.7", {"start": v(37.52, 15.63) * mm, "end": v(37.56, 15.56) * mm});
            skLineSegment(sketch, "E14.29.8", {"start": v(37.59, 15.48) * mm, "end": v(37.56, 15.56) * mm});
            skArc(sketch, "E14.29.9", {"start": v(37.54, 15.03) * mm, "mid": v(37.62, 15.25) * mm, "end": v(37.59, 15.48) * mm});
            skArc(sketch, "E14.30.0", {"start": v(28.84, 20.8) * mm, "mid": v(29.17, 20.6) * mm, "end": v(29.54, 20.69) * mm});
            skLineSegment(sketch, "E14.30.1", {"start": v(31.2, 21.85) * mm, "end": v(29.54, 20.69) * mm});
            skArc(sketch, "E14.30.2", {"start": v(31.2, 21.85) * mm, "mid": v(32.51, 22.08) * mm, "end": v(33.84, 22.13) * mm});
            skArc(sketch, "E14.30.3", {"start": v(33, 19.05) * mm, "mid": v(33.76, 20.14) * mm, "end": v(34.36, 21.32) * mm});
            skArc(sketch, "E14.30.4", {"start": v(31.23, 18.03) * mm, "mid": v(31, 17.73) * mm, "end": v(31.04, 17.34) * mm});
            skLineSegment(sketch, "E14.30.5", {"start": v(33, 19.05) * mm, "end": v(31.23, 18.03) * mm});
            skArc(sketch, "E14.30.6", {"start": v(34.24, 21.91) * mm, "mid": v(34.06, 22.07) * mm, "end": v(33.84, 22.13) * mm});
            skLineSegment(sketch, "E14.30.7", {"start": v(34.24, 21.91) * mm, "end": v(34.29, 21.84) * mm});
            skLineSegment(sketch, "E14.30.8", {"start": v(34.33, 21.77) * mm, "end": v(34.29, 21.84) * mm});
            skArc(sketch, "E14.30.9", {"start": v(34.36, 21.32) * mm, "mid": v(34.4, 21.55) * mm, "end": v(34.33, 21.77) * mm});
            skArc(sketch, "E14.31.0", {"start": v(24.79, 25.5) * mm, "mid": v(25.15, 25.35) * mm, "end": v(25.5, 25.5) * mm});
            skLineSegment(sketch, "E14.31.1", {"start": v(26.94, 26.94) * mm, "end": v(25.5, 25.5) * mm});
            skArc(sketch, "E14.31.2", {"start": v(26.94, 26.94) * mm, "mid": v(28.19, 27.4) * mm, "end": v(29.48, 27.67) * mm});
            skArc(sketch, "E14.31.3", {"start": v(29.19, 24.5) * mm, "mid": v(29.75, 25.7) * mm, "end": v(30.13, 26.96) * mm});
            skArc(sketch, "E14.31.4", {"start": v(27.63, 23.18) * mm, "mid": v(27.45, 22.84) * mm, "end": v(27.56, 22.47) * mm});
            skLineSegment(sketch, "E14.31.5", {"start": v(29.19, 24.5) * mm, "end": v(27.63, 23.18) * mm});
            skArc(sketch, "E14.31.6", {"start": v(29.91, 27.53) * mm, "mid": v(29.71, 27.65) * mm, "end": v(29.48, 27.67) * mm});
            skLineSegment(sketch, "E14.31.7", {"start": v(29.91, 27.53) * mm, "end": v(29.97, 27.46) * mm});
            skLineSegment(sketch, "E14.31.8", {"start": v(30.03, 27.4) * mm, "end": v(29.97, 27.46) * mm});
            skArc(sketch, "E14.31.9", {"start": v(30.13, 26.96) * mm, "mid": v(30.13, 27.2) * mm, "end": v(30.03, 27.4) * mm});
            skArc(sketch, "E14.32.0", {"start": v(19.98, 29.41) * mm, "mid": v(20.36, 29.33) * mm, "end": v(20.69, 29.54) * mm});
            skLineSegment(sketch, "E14.32.1", {"start": v(21.85, 31.2) * mm, "end": v(20.69, 29.54) * mm});
            skArc(sketch, "E14.32.2", {"start": v(21.85, 31.2) * mm, "mid": v(23, 31.87) * mm, "end": v(24.23, 32.37) * mm});
            skArc(sketch, "E14.32.3", {"start": v(24.5, 29.19) * mm, "mid": v(24.83, 30.47) * mm, "end": v(25, 31.78) * mm});
            skArc(sketch, "E14.32.4", {"start": v(23.18, 27.63) * mm, "mid": v(23.06, 27.26) * mm, "end": v(23.24, 26.92) * mm});
            skLineSegment(sketch, "E14.32.5", {"start": v(24.5, 29.19) * mm, "end": v(23.18, 27.63) * mm});
            skArc(sketch, "E14.32.6", {"start": v(24.68, 32.3) * mm, "mid": v(24.46, 32.39) * mm, "end": v(24.23, 32.37) * mm});
            skLineSegment(sketch, "E14.32.7", {"start": v(24.68, 32.3) * mm, "end": v(24.75, 32.25) * mm});
            skLineSegment(sketch, "E14.32.8", {"start": v(24.81, 32.2) * mm, "end": v(24.75, 32.25) * mm});
            skArc(sketch, "E14.32.9", {"start": v(25, 31.78) * mm, "mid": v(24.95, 32.01) * mm, "end": v(24.81, 32.2) * mm});
            skArc(sketch, "E14.33.0", {"start": v(14.57, 32.44) * mm, "mid": v(14.96, 32.42) * mm, "end": v(15.24, 32.69) * mm});
            skLineSegment(sketch, "E14.33.1", {"start": v(16.1, 34.53) * mm, "end": v(15.24, 32.69) * mm});
            skArc(sketch, "E14.33.2", {"start": v(16.1, 34.53) * mm, "mid": v(17.12, 35.38) * mm, "end": v(18.24, 36.08) * mm});
            skArc(sketch, "E14.33.3", {"start": v(19.05, 33) * mm, "mid": v(19.16, 34.32) * mm, "end": v(19.1, 35.64) * mm});
            skArc(sketch, "E14.33.4", {"start": v(18.03, 31.23) * mm, "mid": v(17.98, 30.85) * mm, "end": v(18.21, 30.54) * mm});
            skLineSegment(sketch, "E14.33.5", {"start": v(19.05, 33) * mm, "end": v(18.03, 31.23) * mm});
            skArc(sketch, "E14.33.6", {"start": v(18.7, 36.1) * mm, "mid": v(18.47, 36.14) * mm, "end": v(18.24, 36.08) * mm});
            skLineSegment(sketch, "E14.33.7", {"start": v(18.7, 36.1) * mm, "end": v(18.77, 36.06) * mm});
            skLineSegment(sketch, "E14.33.8", {"start": v(18.85, 36.02) * mm, "end": v(18.77, 36.06) * mm});
            skArc(sketch, "E14.33.9", {"start": v(19.1, 35.64) * mm, "mid": v(19.01, 35.86) * mm, "end": v(18.85, 36.02) * mm});
            skArc(sketch, "E14.34.0", {"start": v(8.72, 34.47) * mm, "mid": v(9.1, 34.53) * mm, "end": v(9.33, 34.84) * mm});
            skLineSegment(sketch, "E14.34.1", {"start": v(9.86, 36.8) * mm, "end": v(9.33, 34.84) * mm});
            skArc(sketch, "E14.34.2", {"start": v(9.86, 36.8) * mm, "mid": v(10.71, 37.82) * mm, "end": v(11.7, 38.7) * mm});
            skArc(sketch, "E14.34.3", {"start": v(13.03, 35.8) * mm, "mid": v(12.91, 37.12) * mm, "end": v(12.62, 38.41) * mm});
            skArc(sketch, "E14.34.4", {"start": v(12.33, 33.89) * mm, "mid": v(12.35, 33.5) * mm, "end": v(12.63, 33.24) * mm});
            skLineSegment(sketch, "E14.34.5", {"start": v(13.03, 35.8) * mm, "end": v(12.33, 33.89) * mm});
            skArc(sketch, "E14.34.6", {"start": v(12.14, 38.8) * mm, "mid": v(11.9, 38.8) * mm, "end": v(11.7, 38.7) * mm});
            skLineSegment(sketch, "E14.34.7", {"start": v(12.14, 38.8) * mm, "end": v(12.22, 38.77) * mm});
            skLineSegment(sketch, "E14.34.8", {"start": v(12.3, 38.74) * mm, "end": v(12.22, 38.77) * mm});
            skArc(sketch, "E14.34.9", {"start": v(12.62, 38.41) * mm, "mid": v(12.5, 38.61) * mm, "end": v(12.3, 38.74) * mm});
            skArc(sketch, "E14.35.0", {"start": v(2.6, 35.46) * mm, "mid": v(2.97, 35.58) * mm, "end": v(3.14, 35.93) * mm});
            skLineSegment(sketch, "E14.35.1", {"start": v(3.32, 37.96) * mm, "end": v(3.14, 35.93) * mm});
            skArc(sketch, "E14.35.2", {"start": v(3.32, 37.96) * mm, "mid": v(3.98, 39.1) * mm, "end": v(4.8, 40.15) * mm});
            skArc(sketch, "E14.35.3", {"start": v(6.62, 37.52) * mm, "mid": v(6.27, 38.8) * mm, "end": v(5.75, 40.02) * mm});
            skArc(sketch, "E14.35.4", {"start": v(6.26, 35.52) * mm, "mid": v(6.34, 35.14) * mm, "end": v(6.67, 34.93) * mm});
            skLineSegment(sketch, "E14.35.5", {"start": v(6.62, 37.52) * mm, "end": v(6.26, 35.52) * mm});
            skArc(sketch, "E14.35.6", {"start": v(5.22, 40.31) * mm, "mid": v(5, 40.28) * mm, "end": v(4.8, 40.15) * mm});
            skLineSegment(sketch, "E14.35.7", {"start": v(5.22, 40.31) * mm, "end": v(5.3, 40.3) * mm});
            skLineSegment(sketch, "E14.35.8", {"start": v(5.4, 40.3) * mm, "end": v(5.3, 40.3) * mm});
            skArc(sketch, "E14.35.9", {"start": v(5.75, 40.02) * mm, "mid": v(5.6, 40.2) * mm, "end": v(5.4, 40.3) * mm});
            skSolve(sketch);
        }
        {
            var Q0;
            Q0 = qSketchRegion(id + "F0", true);
            extrude(context, id + "F1", {"entities" : qUnion([Q0]), "depth" : 6.35 * mm});
        }
        {
            var Q0;
            Q0=makeQuery(id+"F1.opExtrude","CAP_FACE",FACE,{"disambiguationData":[OSD([sQuery(id+"F0.wireOp",EDGE,"E0"),sQuery(id+"F0.wireOp",EDGE,"E2"),sQuery(id+"F0.wireOp",EDGE,"E3"),sQuery(id+"F0.wireOp",EDGE,"E4"),sQuery(id+"F0.wireOp",EDGE,"E5.MirrorCS"),sQuery(id+"F0.wireOp",EDGE,"E6.MirrorCS"),sQuery(id+"F0.wireOp",EDGE,"E7.MirrorCS"),sQuery(id+"F0.wireOp",EDGE,"E10.filletArc"),sQuery(id+"F0.wireOp",EDGE,"E11.filletArc"),sQuery(id+"F0.wireOp",EDGE,"E12.filletArc"),sQuery(id+"F0.wireOp",EDGE,"E13.filletArc"),sQuery(id+"F0.wireOp",EDGE,"E14.1.0"),sQuery(id+"F0.wireOp",EDGE,"E14.1.1"),sQuery(id+"F0.wireOp",EDGE,"E14.1.2"),sQuery(id+"F0.wireOp",EDGE,"E14.1.3"),sQuery(id+"F0.wireOp",EDGE,"E14.1.4"),sQuery(id+"F0.wireOp",EDGE,"E14.1.5"),sQuery(id+"F0.wireOp",EDGE,"E14.1.6"),sQuery(id+"F0.wireOp",EDGE,"E14.1.7"),sQuery(id+"F0.wireOp",EDGE,"E14.1.8"),sQuery(id+"F0.wireOp",EDGE,"E14.1.9"),sQuery(id+"F0.wireOp",EDGE,"E14.2.0"),sQuery(id+"F0.wireOp",EDGE,"E14.2.1"),sQuery(id+"F0.wireOp",EDGE,"E14.2.2"),sQuery(id+"F0.wireOp",EDGE,"E14.2.3"),sQuery(id+"F0.wireOp",EDGE,"E14.2.4"),sQuery(id+"F0.wireOp",EDGE,"E14.2.5"),sQuery(id+"F0.wireOp",EDGE,"E14.2.6"),sQuery(id+"F0.wireOp",EDGE,"E14.2.7"),sQuery(id+"F0.wireOp",EDGE,"E14.2.8"),sQuery(id+"F0.wireOp",EDGE,"E14.2.9"),sQuery(id+"F0.wireOp",EDGE,"E14.3.0"),sQuery(id+"F0.wireOp",EDGE,"E14.3.1"),sQuery(id+"F0.wireOp",EDGE,"E14.3.2"),sQuery(id+"F0.wireOp",EDGE,"E14.3.3"),sQuery(id+"F0.wireOp",EDGE,"E14.3.4"),sQuery(id+"F0.wireOp",EDGE,"E14.3.5"),sQuery(id+"F0.wireOp",EDGE,"E14.3.6"),sQuery(id+"F0.wireOp",EDGE,"E14.3.7"),sQuery(id+"F0.wireOp",EDGE,"E14.3.8"),sQuery(id+"F0.wireOp",EDGE,"E14.3.9"),sQuery(id+"F0.wireOp",EDGE,"E14.4.0"),sQuery(id+"F0.wireOp",EDGE,"E14.4.1"),sQuery(id+"F0.wireOp",EDGE,"E14.4.2"),sQuery(id+"F0.wireOp",EDGE,"E14.4.3"),sQuery(id+"F0.wireOp",EDGE,"E14.4.4"),sQuery(id+"F0.wireOp",EDGE,"E14.4.5"),sQuery(id+"F0.wireOp",EDGE,"E14.4.6"),sQuery(id+"F0.wireOp",EDGE,"E14.4.7"),sQuery(id+"F0.wireOp",EDGE,"E14.4.8"),sQuery(id+"F0.wireOp",EDGE,"E14.4.9"),sQuery(id+"F0.wireOp",EDGE,"E14.5.0"),sQuery(id+"F0.wireOp",EDGE,"E14.5.1"),sQuery(id+"F0.wireOp",EDGE,"E14.5.2"),sQuery(id+"F0.wireOp",EDGE,"E14.5.3"),sQuery(id+"F0.wireOp",EDGE,"E14.5.4"),sQuery(id+"F0.wireOp",EDGE,"E14.5.5"),sQuery(id+"F0.wireOp",EDGE,"E14.5.6"),sQuery(id+"F0.wireOp",EDGE,"E14.5.7"),sQuery(id+"F0.wireOp",EDGE,"E14.5.8"),sQuery(id+"F0.wireOp",EDGE,"E14.5.9"),sQuery(id+"F0.wireOp",EDGE,"E14.6.0"),sQuery(id+"F0.wireOp",EDGE,"E14.6.1"),sQuery(id+"F0.wireOp",EDGE,"E14.6.2"),sQuery(id+"F0.wireOp",EDGE,"E14.6.3"),sQuery(id+"F0.wireOp",EDGE,"E14.6.4"),sQuery(id+"F0.wireOp",EDGE,"E14.6.5"),sQuery(id+"F0.wireOp",EDGE,"E14.6.6"),sQuery(id+"F0.wireOp",EDGE,"E14.6.7"),sQuery(id+"F0.wireOp",EDGE,"E14.6.8"),sQuery(id+"F0.wireOp",EDGE,"E14.6.9"),sQuery(id+"F0.wireOp",EDGE,"E14.7.0"),sQuery(id+"F0.wireOp",EDGE,"E14.7.1"),sQuery(id+"F0.wireOp",EDGE,"E14.7.2"),sQuery(id+"F0.wireOp",EDGE,"E14.7.3"),sQuery(id+"F0.wireOp",EDGE,"E14.7.4"),sQuery(id+"F0.wireOp",EDGE,"E14.7.5"),sQuery(id+"F0.wireOp",EDGE,"E14.7.6"),sQuery(id+"F0.wireOp",EDGE,"E14.7.7"),sQuery(id+"F0.wireOp",EDGE,"E14.7.8"),sQuery(id+"F0.wireOp",EDGE,"E14.7.9"),sQuery(id+"F0.wireOp",EDGE,"E14.8.0"),sQuery(id+"F0.wireOp",EDGE,"E14.8.1"),sQuery(id+"F0.wireOp",EDGE,"E14.8.2"),sQuery(id+"F0.wireOp",EDGE,"E14.8.3"),sQuery(id+"F0.wireOp",EDGE,"E14.8.4"),sQuery(id+"F0.wireOp",EDGE,"E14.8.5"),sQuery(id+"F0.wireOp",EDGE,"E14.8.6"),sQuery(id+"F0.wireOp",EDGE,"E14.8.7"),sQuery(id+"F0.wireOp",EDGE,"E14.8.8"),sQuery(id+"F0.wireOp",EDGE,"E14.8.9"),sQuery(id+"F0.wireOp",EDGE,"E14.9.0"),sQuery(id+"F0.wireOp",EDGE,"E14.9.1"),sQuery(id+"F0.wireOp",EDGE,"E14.9.2"),sQuery(id+"F0.wireOp",EDGE,"E14.9.3"),sQuery(id+"F0.wireOp",EDGE,"E14.9.4"),sQuery(id+"F0.wireOp",EDGE,"E14.9.5"),sQuery(id+"F0.wireOp",EDGE,"E14.9.6"),sQuery(id+"F0.wireOp",EDGE,"E14.9.7"),sQuery(id+"F0.wireOp",EDGE,"E14.9.8"),sQuery(id+"F0.wireOp",EDGE,"E14.9.9"),sQuery(id+"F0.wireOp",EDGE,"E14.10.0"),sQuery(id+"F0.wireOp",EDGE,"E14.10.1"),sQuery(id+"F0.wireOp",EDGE,"E14.10.2"),sQuery(id+"F0.wireOp",EDGE,"E14.10.3"),sQuery(id+"F0.wireOp",EDGE,"E14.10.4"),sQuery(id+"F0.wireOp",EDGE,"E14.10.5"),sQuery(id+"F0.wireOp",EDGE,"E14.10.6"),sQuery(id+"F0.wireOp",EDGE,"E14.10.7"),sQuery(id+"F0.wireOp",EDGE,"E14.10.8"),sQuery(id+"F0.wireOp",EDGE,"E14.10.9"),sQuery(id+"F0.wireOp",EDGE,"E14.11.0"),sQuery(id+"F0.wireOp",EDGE,"E14.11.1"),sQuery(id+"F0.wireOp",EDGE,"E14.11.2"),sQuery(id+"F0.wireOp",EDGE,"E14.11.3"),sQuery(id+"F0.wireOp",EDGE,"E14.11.4"),sQuery(id+"F0.wireOp",EDGE,"E14.11.5"),sQuery(id+"F0.wireOp",EDGE,"E14.11.6"),sQuery(id+"F0.wireOp",EDGE,"E14.11.7"),sQuery(id+"F0.wireOp",EDGE,"E14.11.8"),sQuery(id+"F0.wireOp",EDGE,"E14.11.9"),sQuery(id+"F0.wireOp",EDGE,"E14.12.0"),sQuery(id+"F0.wireOp",EDGE,"E14.12.1"),sQuery(id+"F0.wireOp",EDGE,"E14.12.2"),sQuery(id+"F0.wireOp",EDGE,"E14.12.3"),sQuery(id+"F0.wireOp",EDGE,"E14.12.4"),sQuery(id+"F0.wireOp",EDGE,"E14.12.5"),sQuery(id+"F0.wireOp",EDGE,"E14.12.6"),sQuery(id+"F0.wireOp",EDGE,"E14.12.7"),sQuery(id+"F0.wireOp",EDGE,"E14.12.8"),sQuery(id+"F0.wireOp",EDGE,"E14.12.9"),sQuery(id+"F0.wireOp",EDGE,"E14.13.0"),sQuery(id+"F0.wireOp",EDGE,"E14.13.1"),sQuery(id+"F0.wireOp",EDGE,"E14.13.2"),sQuery(id+"F0.wireOp",EDGE,"E14.13.3"),sQuery(id+"F0.wireOp",EDGE,"E14.13.4"),sQuery(id+"F0.wireOp",EDGE,"E14.13.5"),sQuery(id+"F0.wireOp",EDGE,"E14.13.6"),sQuery(id+"F0.wireOp",EDGE,"E14.13.7"),sQuery(id+"F0.wireOp",EDGE,"E14.13.8"),sQuery(id+"F0.wireOp",EDGE,"E14.13.9"),sQuery(id+"F0.wireOp",EDGE,"E14.14.0"),sQuery(id+"F0.wireOp",EDGE,"E14.14.1"),sQuery(id+"F0.wireOp",EDGE,"E14.14.2"),sQuery(id+"F0.wireOp",EDGE,"E14.14.3"),sQuery(id+"F0.wireOp",EDGE,"E14.14.4"),sQuery(id+"F0.wireOp",EDGE,"E14.14.5"),sQuery(id+"F0.wireOp",EDGE,"E14.14.6"),sQuery(id+"F0.wireOp",EDGE,"E14.14.7"),sQuery(id+"F0.wireOp",EDGE,"E14.14.8"),sQuery(id+"F0.wireOp",EDGE,"E14.14.9"),sQuery(id+"F0.wireOp",EDGE,"E14.15.0"),sQuery(id+"F0.wireOp",EDGE,"E14.15.1"),sQuery(id+"F0.wireOp",EDGE,"E14.15.2"),sQuery(id+"F0.wireOp",EDGE,"E14.15.3"),sQuery(id+"F0.wireOp",EDGE,"E14.15.4"),sQuery(id+"F0.wireOp",EDGE,"E14.15.5"),sQuery(id+"F0.wireOp",EDGE,"E14.15.6"),sQuery(id+"F0.wireOp",EDGE,"E14.15.7"),sQuery(id+"F0.wireOp",EDGE,"E14.15.8"),sQuery(id+"F0.wireOp",EDGE,"E14.15.9"),sQuery(id+"F0.wireOp",EDGE,"E14.16.0"),sQuery(id+"F0.wireOp",EDGE,"E14.16.1"),sQuery(id+"F0.wireOp",EDGE,"E14.16.2"),sQuery(id+"F0.wireOp",EDGE,"E14.16.3"),sQuery(id+"F0.wireOp",EDGE,"E14.16.4"),sQuery(id+"F0.wireOp",EDGE,"E14.16.5"),sQuery(id+"F0.wireOp",EDGE,"E14.16.6"),sQuery(id+"F0.wireOp",EDGE,"E14.16.7"),sQuery(id+"F0.wireOp",EDGE,"E14.16.8"),sQuery(id+"F0.wireOp",EDGE,"E14.16.9"),sQuery(id+"F0.wireOp",EDGE,"E14.17.0"),sQuery(id+"F0.wireOp",EDGE,"E14.17.1"),sQuery(id+"F0.wireOp",EDGE,"E14.17.2"),sQuery(id+"F0.wireOp",EDGE,"E14.17.3"),sQuery(id+"F0.wireOp",EDGE,"E14.17.4"),sQuery(id+"F0.wireOp",EDGE,"E14.17.5"),sQuery(id+"F0.wireOp",EDGE,"E14.17.6"),sQuery(id+"F0.wireOp",EDGE,"E14.17.7"),sQuery(id+"F0.wireOp",EDGE,"E14.17.8"),sQuery(id+"F0.wireOp",EDGE,"E14.17.9"),sQuery(id+"F0.wireOp",EDGE,"E14.18.0"),sQuery(id+"F0.wireOp",EDGE,"E14.18.1"),sQuery(id+"F0.wireOp",EDGE,"E14.18.2"),sQuery(id+"F0.wireOp",EDGE,"E14.18.3"),sQuery(id+"F0.wireOp",EDGE,"E14.18.4"),sQuery(id+"F0.wireOp",EDGE,"E14.18.5"),sQuery(id+"F0.wireOp",EDGE,"E14.18.6"),sQuery(id+"F0.wireOp",EDGE,"E14.18.7"),sQuery(id+"F0.wireOp",EDGE,"E14.18.8"),sQuery(id+"F0.wireOp",EDGE,"E14.18.9"),sQuery(id+"F0.wireOp",EDGE,"E14.19.0"),sQuery(id+"F0.wireOp",EDGE,"E14.19.1"),sQuery(id+"F0.wireOp",EDGE,"E14.19.2"),sQuery(id+"F0.wireOp",EDGE,"E14.19.3"),sQuery(id+"F0.wireOp",EDGE,"E14.19.4"),sQuery(id+"F0.wireOp",EDGE,"E14.19.5"),sQuery(id+"F0.wireOp",EDGE,"E14.19.6"),sQuery(id+"F0.wireOp",EDGE,"E14.19.7"),sQuery(id+"F0.wireOp",EDGE,"E14.19.8"),sQuery(id+"F0.wireOp",EDGE,"E14.19.9"),sQuery(id+"F0.wireOp",EDGE,"E14.20.0"),sQuery(id+"F0.wireOp",EDGE,"E14.20.1"),sQuery(id+"F0.wireOp",EDGE,"E14.20.2"),sQuery(id+"F0.wireOp",EDGE,"E14.20.3"),sQuery(id+"F0.wireOp",EDGE,"E14.20.4"),sQuery(id+"F0.wireOp",EDGE,"E14.20.5"),sQuery(id+"F0.wireOp",EDGE,"E14.20.6"),sQuery(id+"F0.wireOp",EDGE,"E14.20.7"),sQuery(id+"F0.wireOp",EDGE,"E14.20.8"),sQuery(id+"F0.wireOp",EDGE,"E14.20.9"),sQuery(id+"F0.wireOp",EDGE,"E14.21.0"),sQuery(id+"F0.wireOp",EDGE,"E14.21.1"),sQuery(id+"F0.wireOp",EDGE,"E14.21.2"),sQuery(id+"F0.wireOp",EDGE,"E14.21.3"),sQuery(id+"F0.wireOp",EDGE,"E14.21.4"),sQuery(id+"F0.wireOp",EDGE,"E14.21.5"),sQuery(id+"F0.wireOp",EDGE,"E14.21.6"),sQuery(id+"F0.wireOp",EDGE,"E14.21.7"),sQuery(id+"F0.wireOp",EDGE,"E14.21.8"),sQuery(id+"F0.wireOp",EDGE,"E14.21.9"),sQuery(id+"F0.wireOp",EDGE,"E14.22.0"),sQuery(id+"F0.wireOp",EDGE,"E14.22.1"),sQuery(id+"F0.wireOp",EDGE,"E14.22.2"),sQuery(id+"F0.wireOp",EDGE,"E14.22.3"),sQuery(id+"F0.wireOp",EDGE,"E14.22.4"),sQuery(id+"F0.wireOp",EDGE,"E14.22.5"),sQuery(id+"F0.wireOp",EDGE,"E14.22.6"),sQuery(id+"F0.wireOp",EDGE,"E14.22.7"),sQuery(id+"F0.wireOp",EDGE,"E14.22.8"),sQuery(id+"F0.wireOp",EDGE,"E14.22.9"),sQuery(id+"F0.wireOp",EDGE,"E14.23.0"),sQuery(id+"F0.wireOp",EDGE,"E14.23.1"),sQuery(id+"F0.wireOp",EDGE,"E14.23.2"),sQuery(id+"F0.wireOp",EDGE,"E14.23.3"),sQuery(id+"F0.wireOp",EDGE,"E14.23.4"),sQuery(id+"F0.wireOp",EDGE,"E14.23.5"),sQuery(id+"F0.wireOp",EDGE,"E14.23.6"),sQuery(id+"F0.wireOp",EDGE,"E14.23.7"),sQuery(id+"F0.wireOp",EDGE,"E14.23.8"),sQuery(id+"F0.wireOp",EDGE,"E14.23.9"),sQuery(id+"F0.wireOp",EDGE,"E14.24.0"),sQuery(id+"F0.wireOp",EDGE,"E14.24.1"),sQuery(id+"F0.wireOp",EDGE,"E14.24.2"),sQuery(id+"F0.wireOp",EDGE,"E14.24.3"),sQuery(id+"F0.wireOp",EDGE,"E14.24.4"),sQuery(id+"F0.wireOp",EDGE,"E14.24.5"),sQuery(id+"F0.wireOp",EDGE,"E14.24.6"),sQuery(id+"F0.wireOp",EDGE,"E14.24.7"),sQuery(id+"F0.wireOp",EDGE,"E14.24.8"),sQuery(id+"F0.wireOp",EDGE,"E14.24.9"),sQuery(id+"F0.wireOp",EDGE,"E14.25.0"),sQuery(id+"F0.wireOp",EDGE,"E14.25.1"),sQuery(id+"F0.wireOp",EDGE,"E14.25.2"),sQuery(id+"F0.wireOp",EDGE,"E14.25.3"),sQuery(id+"F0.wireOp",EDGE,"E14.25.4"),sQuery(id+"F0.wireOp",EDGE,"E14.25.5"),sQuery(id+"F0.wireOp",EDGE,"E14.25.6"),sQuery(id+"F0.wireOp",EDGE,"E14.25.7"),sQuery(id+"F0.wireOp",EDGE,"E14.25.8"),sQuery(id+"F0.wireOp",EDGE,"E14.25.9"),sQuery(id+"F0.wireOp",EDGE,"E14.26.0"),sQuery(id+"F0.wireOp",EDGE,"E14.26.1"),sQuery(id+"F0.wireOp",EDGE,"E14.26.2"),sQuery(id+"F0.wireOp",EDGE,"E14.26.3"),sQuery(id+"F0.wireOp",EDGE,"E14.26.4"),sQuery(id+"F0.wireOp",EDGE,"E14.26.5"),sQuery(id+"F0.wireOp",EDGE,"E14.26.6"),sQuery(id+"F0.wireOp",EDGE,"E14.26.7"),sQuery(id+"F0.wireOp",EDGE,"E14.26.8"),sQuery(id+"F0.wireOp",EDGE,"E14.26.9"),sQuery(id+"F0.wireOp",EDGE,"E14.27.0"),sQuery(id+"F0.wireOp",EDGE,"E14.27.1"),sQuery(id+"F0.wireOp",EDGE,"E14.27.2"),sQuery(id+"F0.wireOp",EDGE,"E14.27.3"),sQuery(id+"F0.wireOp",EDGE,"E14.27.4"),sQuery(id+"F0.wireOp",EDGE,"E14.27.5"),sQuery(id+"F0.wireOp",EDGE,"E14.27.6"),sQuery(id+"F0.wireOp",EDGE,"E14.27.7"),sQuery(id+"F0.wireOp",EDGE,"E14.27.8"),sQuery(id+"F0.wireOp",EDGE,"E14.27.9"),sQuery(id+"F0.wireOp",EDGE,"E14.28.0"),sQuery(id+"F0.wireOp",EDGE,"E14.28.1"),sQuery(id+"F0.wireOp",EDGE,"E14.28.2"),sQuery(id+"F0.wireOp",EDGE,"E14.28.3"),sQuery(id+"F0.wireOp",EDGE,"E14.28.4"),sQuery(id+"F0.wireOp",EDGE,"E14.28.5"),sQuery(id+"F0.wireOp",EDGE,"E14.28.6"),sQuery(id+"F0.wireOp",EDGE,"E14.28.7"),sQuery(id+"F0.wireOp",EDGE,"E14.28.8"),sQuery(id+"F0.wireOp",EDGE,"E14.28.9"),sQuery(id+"F0.wireOp",EDGE,"E14.29.0"),sQuery(id+"F0.wireOp",EDGE,"E14.29.1"),sQuery(id+"F0.wireOp",EDGE,"E14.29.2"),sQuery(id+"F0.wireOp",EDGE,"E14.29.3"),sQuery(id+"F0.wireOp",EDGE,"E14.29.4"),sQuery(id+"F0.wireOp",EDGE,"E14.29.5"),sQuery(id+"F0.wireOp",EDGE,"E14.29.6"),sQuery(id+"F0.wireOp",EDGE,"E14.29.7"),sQuery(id+"F0.wireOp",EDGE,"E14.29.8"),sQuery(id+"F0.wireOp",EDGE,"E14.29.9"),sQuery(id+"F0.wireOp",EDGE,"E14.30.0"),sQuery(id+"F0.wireOp",EDGE,"E14.30.1"),sQuery(id+"F0.wireOp",EDGE,"E14.30.2"),sQuery(id+"F0.wireOp",EDGE,"E14.30.3"),sQuery(id+"F0.wireOp",EDGE,"E14.30.4"),sQuery(id+"F0.wireOp",EDGE,"E14.30.5"),sQuery(id+"F0.wireOp",EDGE,"E14.30.6"),sQuery(id+"F0.wireOp",EDGE,"E14.30.7"),sQuery(id+"F0.wireOp",EDGE,"E14.30.8"),sQuery(id+"F0.wireOp",EDGE,"E14.30.9"),sQuery(id+"F0.wireOp",EDGE,"E14.31.0"),sQuery(id+"F0.wireOp",EDGE,"E14.31.1"),sQuery(id+"F0.wireOp",EDGE,"E14.31.2"),sQuery(id+"F0.wireOp",EDGE,"E14.31.3"),sQuery(id+"F0.wireOp",EDGE,"E14.31.4"),sQuery(id+"F0.wireOp",EDGE,"E14.31.5"),sQuery(id+"F0.wireOp",EDGE,"E14.31.6"),sQuery(id+"F0.wireOp",EDGE,"E14.31.7"),sQuery(id+"F0.wireOp",EDGE,"E14.31.8"),sQuery(id+"F0.wireOp",EDGE,"E14.31.9"),sQuery(id+"F0.wireOp",EDGE,"E14.32.0"),sQuery(id+"F0.wireOp",EDGE,"E14.32.1"),sQuery(id+"F0.wireOp",EDGE,"E14.32.2"),sQuery(id+"F0.wireOp",EDGE,"E14.32.3"),sQuery(id+"F0.wireOp",EDGE,"E14.32.4"),sQuery(id+"F0.wireOp",EDGE,"E14.32.5"),sQuery(id+"F0.wireOp",EDGE,"E14.32.6"),sQuery(id+"F0.wireOp",EDGE,"E14.32.7"),sQuery(id+"F0.wireOp",EDGE,"E14.32.8"),sQuery(id+"F0.wireOp",EDGE,"E14.32.9"),sQuery(id+"F0.wireOp",EDGE,"E14.33.0"),sQuery(id+"F0.wireOp",EDGE,"E14.33.1"),sQuery(id+"F0.wireOp",EDGE,"E14.33.2"),sQuery(id+"F0.wireOp",EDGE,"E14.33.3"),sQuery(id+"F0.wireOp",EDGE,"E14.33.4"),sQuery(id+"F0.wireOp",EDGE,"E14.33.5"),sQuery(id+"F0.wireOp",EDGE,"E14.33.6"),sQuery(id+"F0.wireOp",EDGE,"E14.33.7"),sQuery(id+"F0.wireOp",EDGE,"E14.33.8"),sQuery(id+"F0.wireOp",EDGE,"E14.33.9"),sQuery(id+"F0.wireOp",EDGE,"E14.34.0"),sQuery(id+"F0.wireOp",EDGE,"E14.34.1"),sQuery(id+"F0.wireOp",EDGE,"E14.34.2"),sQuery(id+"F0.wireOp",EDGE,"E14.34.3"),sQuery(id+"F0.wireOp",EDGE,"E14.34.4"),sQuery(id+"F0.wireOp",EDGE,"E14.34.5"),sQuery(id+"F0.wireOp",EDGE,"E14.34.6"),sQuery(id+"F0.wireOp",EDGE,"E14.34.7"),sQuery(id+"F0.wireOp",EDGE,"E14.34.8"),sQuery(id+"F0.wireOp",EDGE,"E14.34.9"),sQuery(id+"F0.wireOp",EDGE,"E14.35.0"),sQuery(id+"F0.wireOp",EDGE,"E14.35.1"),sQuery(id+"F0.wireOp",EDGE,"E14.35.2"),sQuery(id+"F0.wireOp",EDGE,"E14.35.3"),sQuery(id+"F0.wireOp",EDGE,"E14.35.4"),sQuery(id+"F0.wireOp",EDGE,"E14.35.5"),sQuery(id+"F0.wireOp",EDGE,"E14.35.6"),sQuery(id+"F0.wireOp",EDGE,"E14.35.7"),sQuery(id+"F0.wireOp",EDGE,"E14.35.8"),sQuery(id+"F0.wireOp",EDGE,"E14.35.9")])],"isStart":false});
            var sketch = newSketch(context, id + "F2", { "sketchPlane" : qUnion([Q0])});
            skCircle(sketch, "E15", {"center": v(0, 0) * mm, "radius": 6.35 * mm});
            skSolve(sketch);
        }
        {
            var Q0;
            Q0 = qSketchRegion(id + "F2", true);
            extrude(context, id + "F3", {"entities" : qUnion([Q0]), "operationType" : NewBodyOperationType.REMOVE, "endBound" : BoundingType.THROUGH_ALL, "oppositeDirection" : true, "depth" : 25.4 * mm});
        }
    });
